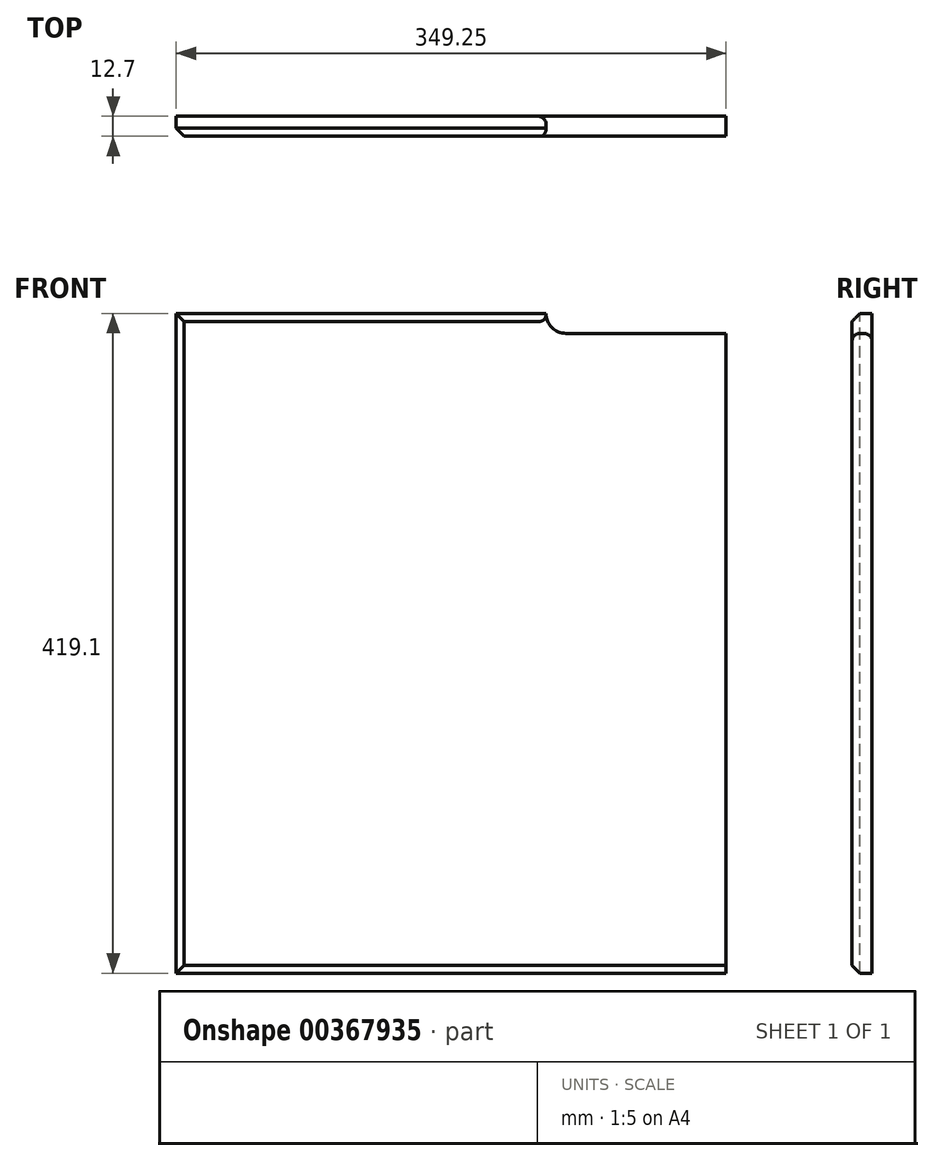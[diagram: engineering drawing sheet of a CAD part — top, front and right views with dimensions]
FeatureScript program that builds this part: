
annotation { "Feature Type Name" : "Feature", "Feature Type Description" : "" }
export const myFeature = defineFeature(function(context is Context, id is Id, definition is map)
    precondition{}
    {
        {
            var Q0;
            Q0=qCreatedBy(makeId("Front.planeOp"),FACE);
            var sketch = newSketch(context, id + "F0", { "sketchPlane" : qUnion([Q0])});
            skLineSegment(sketch, "E0.bottom", {"start": v(-179.4, 244.25) * mm, "end": v(169.86, 244.25) * mm});
            skLineSegment(sketch, "E0.top", {"start": v(-179.4, -174.85) * mm, "end": v(169.86, -174.85) * mm});
            skLineSegment(sketch, "E0.left", {"start": v(-179.4, 244.25) * mm, "end": v(-179.4, -174.85) * mm});
            skLineSegment(sketch, "E0.right", {"start": v(169.86, 244.25) * mm, "end": v(169.86, -174.85) * mm});
            skLineSegment(sketch, "E1", {"start": v(169.86, 244.25) * mm, "end": v(68.26, 244.25) * mm});
            skArc(sketch, "E2.0.endCap", {"start": v(68.26, 231.55) * mm, "mid": v(59.28, 235.26) * mm, "end": v(55.56, 244.25) * mm});
            skLineSegment(sketch, "E2.0.left", {"start": v(169.86, 231.55) * mm, "end": v(68.26, 231.55) * mm});
            skSolve(sketch);
        }
        {
            var Q0;
            {var subQ1=sQuery(id+"F0.wireOp",EDGE,"E0.top");Q0=makeQuery(id+"F0.imprint","IMPRINT",FACE,{"disambiguationData":[TD([[makeQuery(id+"F0.imprint","IMPRINT",EDGE,{"derivedFrom":subQ1}),1.0]])]});}
            extrude(context, id + "F1", {"entities" : qUnion([Q0]), "depth" : 12.7 * mm});
        }
        {
            var Q0;
            Q0=makeQuery(id+"F1.opExtrude","CAP_EDGE",EDGE,{"disambiguationData":[OSD([sQuery(id+"F0.wireOp",EDGE,"E2.0.left")])],"isStart":true});
            var Q1;
            Q1=makeQuery(id+"F1.opExtrude","CAP_EDGE",EDGE,{"disambiguationData":[OSD([sQuery(id+"F0.wireOp",EDGE,"E2.0.left")])],"isStart":false});
            fillet(context, id + "F2", {"entities" : qUnion([Q0, Q1]), "radius" : 5.08 * mm, "tangentPropagation" : true, "allowEdgeOverflow" : false});
        }
        {
            var Q0;
            Q0=makeQuery(id+"F1.opExtrude","CAP_EDGE",EDGE,{"disambiguationData":[OSD([sQuery(id+"F0.wireOp",EDGE,"E0.left")])],"isStart":false});
            var Q1;
            Q1=makeQuery(id+"F1.opExtrude","CAP_EDGE",EDGE,{"disambiguationData":[OSD([sQuery(id+"F0.wireOp",EDGE,"E0.top")])],"isStart":false});
            chamfer(context, id + "F3", {"entities" : qUnion([Q0, Q1]), "width" : 5.08 * mm});
        }
        {
            var Q0;
            Q0=makeQuery(id+"F1.opExtrude","CAP_EDGE",EDGE,{"disambiguationData":[OSD([sQuery(id+"F0.wireOp",EDGE,"E0.bottom")])],"isStart":false});
            chamfer(context, id + "F4", {"entities" : qUnion([Q0]), "width" : 5.08 * mm});
        }
    });
